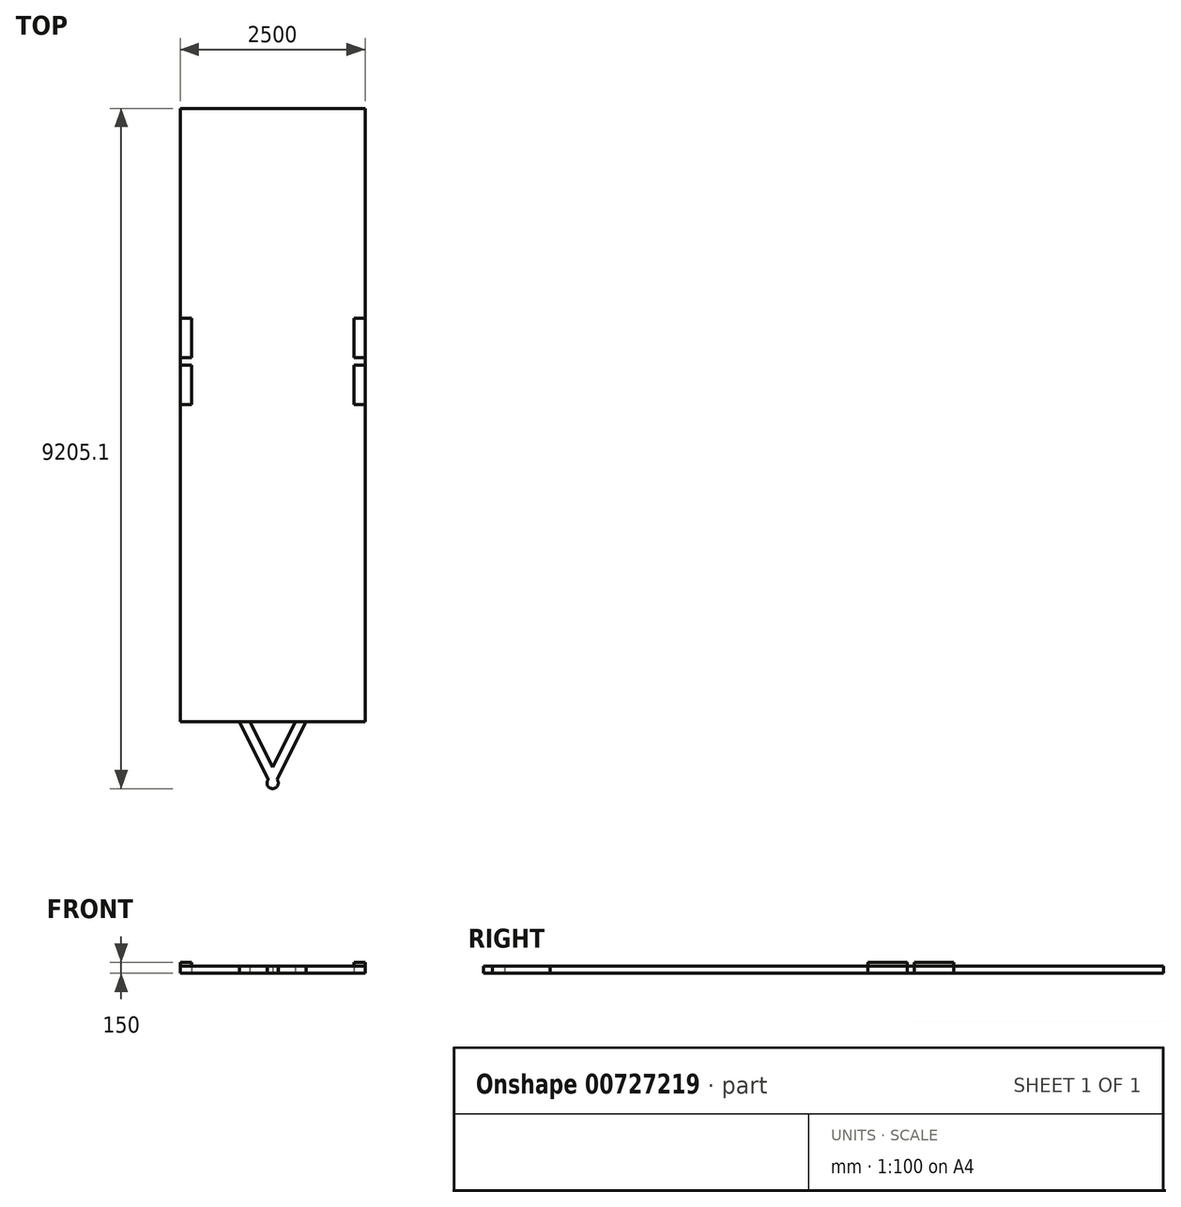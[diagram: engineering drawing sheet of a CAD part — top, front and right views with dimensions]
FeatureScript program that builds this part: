
annotation { "Feature Type Name" : "Feature", "Feature Type Description" : "" }
export const myFeature = defineFeature(function(context is Context, id is Id, definition is map)
    precondition{}
    {
        {
            var Q0;
            Q0=qCreatedBy(makeId("Top.planeOp"),FACE);
            var sketch = newSketch(context, id + "F0", { "sketchPlane" : qUnion([Q0])});
            skLineSegment(sketch, "E0.bottom", {"start": v(1250, -4150) * mm, "end": v(-1250, -4150) * mm});
            skLineSegment(sketch, "E0.top", {"start": v(1250, 4150) * mm, "end": v(-1250, 4150) * mm});
            skLineSegment(sketch, "E0.left", {"start": v(1250, -4150) * mm, "end": v(1250, 4150) * mm});
            skLineSegment(sketch, "E0.right", {"start": v(-1250, -4150) * mm, "end": v(-1250, 4150) * mm});
            skPoint(sketch, "E0.middle", {"position": v(0, 0) * mm});
            skSolve(sketch);
        }
        {
            var Q0;
            Q0=makeQuery(id+"F0.imprint","IMPRINT",FACE,{"disambiguationData":[TD([[makeQuery(id+"F0.imprint","IMPRINT",EDGE,{"derivedFrom":sQuery(id+"F0.wireOp",EDGE,"E0.bottom")}),-1.0]])]});
            extrude(context, id + "F1", {"entities" : qUnion([Q0]), "depth" : 100 * mm, "offsetDistance" : 25 * mm});
        }
        {
            var Q0;
            Q0=qCreatedBy(makeId("Top.planeOp"),FACE);
            var sketch = newSketch(context, id + "F2", { "sketchPlane" : qUnion([Q0])});
            skLineSegment(sketch, "E1", {"start": v(-450, -4150) * mm, "end": v(0, -5050) * mm});
            skLineSegment(sketch, "E2", {"start": v(0, -5050) * mm, "end": v(450, -4150) * mm});
            skLineSegment(sketch, "E3", {"start": v(-450, -4150) * mm, "end": v(-308, -4150) * mm});
            skLineSegment(sketch, "E4", {"start": v(-308, -4150) * mm, "end": v(0, -4766.02) * mm});
            skLineSegment(sketch, "E5", {"start": v(0, -4766.02) * mm, "end": v(308, -4150) * mm});
            skLineSegment(sketch, "E6", {"start": v(308, -4150) * mm, "end": v(450, -4150) * mm});
            skCircle(sketch, "E7", {"center": v(0, -4978.9) * mm, "radius": 76.2 * mm});
            skSolve(sketch);
        }
        {
            var Q0;
            Q0=makeQuery(id+"F2.imprint","IMPRINT",FACE,{"disambiguationData":[TD([[makeQuery(id+"F2.imprint","IMPRINT",EDGE,{"derivedFrom":sQuery(id+"F2.wireOp",EDGE,"E1")}),1.0]])]});
            var Q1;
            {var subQ0=sQuery(id+"F2.wireOp",EDGE,"E3");Q1=makeQuery(id+"F2.imprint","IMPRINT",FACE,{"disambiguationData":[TD([[makeQuery(id+"F2.imprint","IMPRINT",EDGE,{"derivedFrom":subQ0}),-1.0]])]});}
            var Q2;
            {var subQ3=sQuery(id+"F2.wireOp",EDGE,"E7");var subQ9=sQuery(id+"F2.wireOp",EDGE,"E1");var subQ10=makeQuery(id+"F2.imprint","INTERSECT",VERTEX,{"disambiguationData":[OD(0.0)],"derivedFrom":[subQ9,subQ3]});Q2=makeQuery(id+"F2.imprint","IMPRINT",FACE,{"disambiguationData":[TD([[makeQuery(id+"F2.imprint","IMPRINT",EDGE,{"disambiguationData":[TD([[subQ10,-1.0]])],"derivedFrom":subQ9}),1.0]])]});}
            var Q3;
            {var subQ0=sQuery(id+"F2.wireOp",EDGE,"E7");var subQ1=sQuery(id+"F2.wireOp",EDGE,"E1");var subQ2=makeQuery(id+"F2.imprint","INTERSECT",VERTEX,{"disambiguationData":[OD(0.0)],"derivedFrom":[subQ1,subQ0]});Q3=makeQuery(id+"F2.imprint","IMPRINT",FACE,{"disambiguationData":[TD([[makeQuery(id+"F2.imprint","IMPRINT",EDGE,{"disambiguationData":[TD([[subQ2,-1.0]])],"derivedFrom":subQ1}),-1.0]])]});}
            var Q4;
            {var subQ0=sQuery(id+"F2.wireOp",EDGE,"E7");var subQ1=sQuery(id+"F2.wireOp",EDGE,"E2");var subQ2=makeQuery(id+"F2.imprint","INTERSECT",VERTEX,{"disambiguationData":[OD(0.0)],"derivedFrom":[subQ1,subQ0]});Q4=makeQuery(id+"F2.imprint","IMPRINT",FACE,{"disambiguationData":[TD([[makeQuery(id+"F2.imprint","IMPRINT",EDGE,{"disambiguationData":[TD([[subQ2,-1.0]])],"derivedFrom":subQ1}),-1.0]])]});}
            var Q5;
            {var subQ0=sQuery(id+"F2.wireOp",EDGE,"E6");Q5=makeQuery(id+"F2.imprint","IMPRINT",FACE,{"disambiguationData":[TD([[makeQuery(id+"F2.imprint","IMPRINT",EDGE,{"derivedFrom":subQ0}),-1.0]])]});}
            extrude(context, id + "F3", {"entities" : qUnion([Q0, Q1, Q2, Q3, Q4, Q5]), "depth" : 100 * mm, "offsetDistance" : 25 * mm});
        }
        {
            var Q0;
            Q0=qCreatedBy(makeId("Top.planeOp"),FACE);
            var sketch = newSketch(context, id + "F4", { "sketchPlane" : qUnion([Q0])});
            skLineSegment(sketch, "E8", {"start": v(-1250, 730) * mm, "end": v(1250, 730) * mm, "construction": true});
            skLineSegment(sketch, "E9.bottom", {"start": v(-1250, 1313.4) * mm, "end": v(-1097.6, 1313.4) * mm});
            skLineSegment(sketch, "E9.top", {"start": v(-1250, 780) * mm, "end": v(-1097.6, 780) * mm});
            skLineSegment(sketch, "E9.left", {"start": v(-1250, 1313.4) * mm, "end": v(-1250, 780) * mm});
            skLineSegment(sketch, "E9.right", {"start": v(-1097.6, 1313.4) * mm, "end": v(-1097.6, 780) * mm});
            skLineSegment(sketch, "E10.MirrorCS", {"start": v(-1250, 146.6) * mm, "end": v(-1097.6, 146.6) * mm});
            skLineSegment(sketch, "E11.MirrorCS", {"start": v(-1250, 680) * mm, "end": v(-1097.6, 680) * mm});
            skLineSegment(sketch, "E12.MirrorCS", {"start": v(-1250, 146.6) * mm, "end": v(-1250, 680) * mm});
            skLineSegment(sketch, "E13.MirrorCS", {"start": v(-1097.6, 146.6) * mm, "end": v(-1097.6, 680) * mm});
            skLineSegment(sketch, "E14", {"start": v(0, 0) * mm, "end": v(0, 1513.06) * mm, "construction": true});
            skLineSegment(sketch, "E15.MirrorCS", {"start": v(1250, 146.6) * mm, "end": v(1250, 680) * mm});
            skLineSegment(sketch, "E16.MirrorCS", {"start": v(1250, 146.6) * mm, "end": v(1097.6, 146.6) * mm});
            skLineSegment(sketch, "E17.MirrorCS", {"start": v(1097.6, 1313.4) * mm, "end": v(1097.6, 780) * mm});
            skLineSegment(sketch, "E18.MirrorCS", {"start": v(1097.6, 146.6) * mm, "end": v(1097.6, 680) * mm});
            skLineSegment(sketch, "E19.MirrorCS", {"start": v(1250, 1313.4) * mm, "end": v(1250, 780) * mm});
            skLineSegment(sketch, "E20.MirrorCS", {"start": v(1250, 1313.4) * mm, "end": v(1097.6, 1313.4) * mm});
            skLineSegment(sketch, "E21.MirrorCS", {"start": v(1250, 780) * mm, "end": v(1097.6, 780) * mm});
            skLineSegment(sketch, "E22.MirrorCS", {"start": v(1250, 680) * mm, "end": v(1097.6, 680) * mm});
            skSolve(sketch);
        }
        {
            var Q0;
            Q0 = qSketchRegion(id + "F4", true);
            extrude(context, id + "F5", {"entities" : qUnion([Q0]), "depth" : 150 * mm, "offsetDistance" : 25 * mm});
        }
    });
